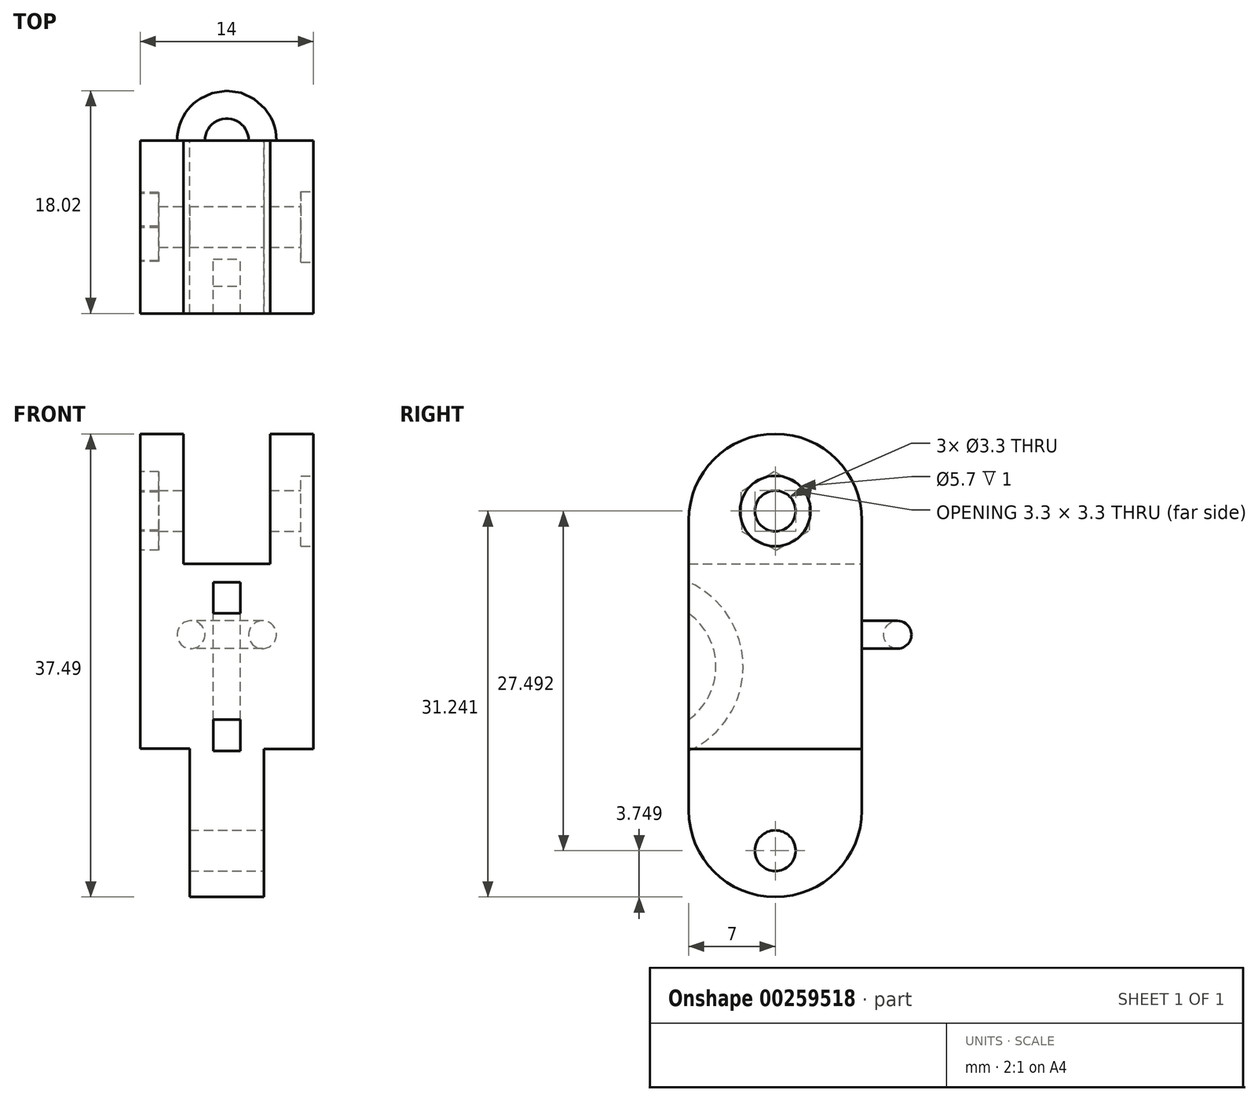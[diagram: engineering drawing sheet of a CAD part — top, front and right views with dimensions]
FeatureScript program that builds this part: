
annotation { "Feature Type Name" : "Feature", "Feature Type Description" : "" }
export const myFeature = defineFeature(function(context is Context, id is Id, definition is map)
    precondition{}
    {
        {
            var Q0;
            Q0=qCreatedBy(makeId("Front.planeOp"),FACE);
            var sketch = newSketch(context, id + "F0", { "sketchPlane" : qUnion([Q0])});
            skLineSegment(sketch, "E0.left", {"start": v(-39.5, 21.54) * mm, "end": v(-39.5, -1.95) * mm});
            skLineSegment(sketch, "E0.right", {"start": v(-25.5, 21.54) * mm, "end": v(-25.5, -1.98) * mm});
            skLineSegment(sketch, "E1.left", {"start": v(-39.5, 21.54) * mm, "end": v(-39.5, 21.54) * mm});
            skLineSegment(sketch, "E2", {"start": v(-36, 21.54) * mm, "end": v(-36, 13.03) * mm});
            skLineSegment(sketch, "E3", {"start": v(-36, 13.03) * mm, "end": v(-29, 13.03) * mm});
            skLineSegment(sketch, "E4", {"start": v(-29, 13.03) * mm, "end": v(-29, 21.53) * mm});
            skPoint(sketch, "E5", {"position": v(-29, 17.28) * mm});
            skLineSegment(sketch, "E6", {"start": v(-35.5, -6.45) * mm, "end": v(-35.5, -13.95) * mm});
            skLineSegment(sketch, "E7", {"start": v(-35.5, -13.95) * mm, "end": v(-29.5, -13.95) * mm});
            skLineSegment(sketch, "E8", {"start": v(-29.5, -13.95) * mm, "end": v(-29.5, -6.48) * mm});
            skLineSegment(sketch, "E9", {"start": v(-35.5, -6.45) * mm, "end": v(-29.5, -6.48) * mm});
            skLineSegment(sketch, "E10", {"start": v(-35.5, -3.45) * mm, "end": v(-35.5, -6.45) * mm});
            skLineSegment(sketch, "E11", {"start": v(-29.5, -6.48) * mm, "end": v(-29.5, -3.48) * mm});
            skPoint(sketch, "E12", {"position": v(-29.5, -10.22) * mm});
            skLineSegment(sketch, "E13", {"start": v(-39.5, 21.54) * mm, "end": v(-39.5, 23.54) * mm});
            skLineSegment(sketch, "E14", {"start": v(-36, 21.54) * mm, "end": v(-36, 23.54) * mm});
            skLineSegment(sketch, "E15", {"start": v(-36, 23.54) * mm, "end": v(-39.5, 23.54) * mm});
            skLineSegment(sketch, "E16", {"start": v(-29, 21.53) * mm, "end": v(-29, 23.54) * mm});
            skLineSegment(sketch, "E17", {"start": v(-25.5, 21.54) * mm, "end": v(-25.5, 23.54) * mm});
            skLineSegment(sketch, "E18", {"start": v(-25.5, 23.54) * mm, "end": v(-29, 23.54) * mm});
            skLineSegment(sketch, "E19", {"start": v(-35.5, -3.45) * mm, "end": v(-35.5, -1.95) * mm});
            skLineSegment(sketch, "E20", {"start": v(-35.5, -1.95) * mm, "end": v(-39.5, -1.95) * mm});
            skLineSegment(sketch, "E21", {"start": v(-29.5, -3.48) * mm, "end": v(-29.5, -1.98) * mm});
            skLineSegment(sketch, "E22", {"start": v(-29.5, -1.98) * mm, "end": v(-25.5, -1.98) * mm});
            skSolve(sketch);
        }
        {
            var Q0;
            Q0=makeQuery(id+"F0.imprint","IMPRINT",FACE,{"disambiguationData":[TD([[makeQuery(id+"F0.imprint","IMPRINT",EDGE,{"derivedFrom":sQuery(id+"F0.wireOp",EDGE,"E0.top")}),1.0]])]});
            var Q1;
            Q1=makeQuery(id+"F0.imprint","IMPRINT",FACE,{"disambiguationData":[TD([[makeQuery(id+"F0.imprint","IMPRINT",EDGE,{"derivedFrom":sQuery(id+"F0.wireOp",EDGE,"ADavjHGe-tSKU-QmEj-BJW0-Q7HaZQKlhmP1")}),1.0]])]});
            var Q2;
            Q2=makeQuery(id+"F0.imprint","IMPRINT",FACE,{"disambiguationData":[TD([[makeQuery(id+"F0.imprint","IMPRINT",EDGE,{"derivedFrom":sQuery(id+"F0.wireOp",EDGE,"E0.left")}),1.0]])]});
            var Q3;
            Q3=makeQuery(id+"F0.imprint","IMPRINT",FACE,{"disambiguationData":[TD([[makeQuery(id+"F0.imprint","IMPRINT",EDGE,{"derivedFrom":sQuery(id+"F0.wireOp",EDGE,"E6")}),1.0]])]});
            extrude(context, id + "F1", {"entities" : qUnion([Q0, Q1, Q2, Q3]), "endBound" : BoundingType.SYMMETRIC, "depth" : 14 * mm});
        }
        {
            var Q0;
            Q0=makeQuery(id+"F1.opExtrude","SWEPT_FACE",FACE,{"disambiguationData":[OSD([sQuery(id+"F0.wireOp",EDGE,"E8")])]});
            var sketch = newSketch(context, id + "F2", { "sketchPlane" : qUnion([Q0])});
            skCircle(sketch, "E23", {"center": v(0, -10.2) * mm, "radius": 1.65 * mm});
            skSolve(sketch);
        }
        {
            var Q0;
            Q0 = qSketchRegion(id + "F2", true);
            extrude(context, id + "F3", {"entities" : qUnion([Q0]), "operationType" : NewBodyOperationType.REMOVE, "oppositeDirection" : true, "depth" : 25 * mm});
        }
        {
            var Q0;
            Q0=makeQuery(id+"F1.opExtrude","SWEPT_FACE",FACE,{"disambiguationData":[OSD([sQuery(id+"F0.wireOp",EDGE,"E0.right")])]});
            var sketch = newSketch(context, id + "F4", { "sketchPlane" : qUnion([Q0])});
            skCircle(sketch, "E24", {"center": v(0, 17.3) * mm, "radius": 1.65 * mm});
            skSolve(sketch);
        }
        {
            var Q0;
            Q0 = qSketchRegion(id + "F4", true);
            extrude(context, id + "F5", {"entities" : qUnion([Q0]), "operationType" : NewBodyOperationType.REMOVE, "oppositeDirection" : true, "depth" : 25 * mm});
        }
        {
            var Q0;
            Q0=makeQuery(id+"F1.opExtrude","CAP_EDGE",EDGE,{"disambiguationData":[OSD([sQuery(id+"F0.wireOp",EDGE,"E15")])],"isStart":false});
            var Q1;
            Q1=makeQuery(id+"F1.opExtrude","CAP_EDGE",EDGE,{"disambiguationData":[OSD([sQuery(id+"F0.wireOp",EDGE,"E15")])],"isStart":true});
            var Q2;
            Q2=makeQuery(id+"F1.opExtrude","CAP_EDGE",EDGE,{"disambiguationData":[OSD([sQuery(id+"F0.wireOp",EDGE,"E18")])],"isStart":true});
            var Q3;
            Q3=makeQuery(id+"F1.opExtrude","CAP_EDGE",EDGE,{"disambiguationData":[OSD([sQuery(id+"F0.wireOp",EDGE,"E18")])],"isStart":false});
            var Q4;
            Q4=makeQuery(id+"F1.opExtrude","CAP_EDGE",EDGE,{"disambiguationData":[OSD([sQuery(id+"F0.wireOp",EDGE,"E7")])],"isStart":false});
            var Q5;
            Q5=makeQuery(id+"F1.opExtrude","CAP_EDGE",EDGE,{"disambiguationData":[OSD([sQuery(id+"F0.wireOp",EDGE,"E7")])],"isStart":true});
            fillet(context, id + "F6", {"entities" : qUnion([Q0, Q1, Q2, Q3, Q4, Q5]), "radius" : 7 * mm, "tangentPropagation" : true, "allowEdgeOverflow" : false});
        }
        {
            var Q0;
            Q0=makeQuery(id+"F1.opExtrude","SWEPT_FACE",FACE,{"disambiguationData":[OSD([sQuery(id+"F0.wireOp",EDGE,"E0.right")])]});
            var sketch = newSketch(context, id + "F7", { "sketchPlane" : qUnion([Q0])});
            skCircle(sketch, "E25", {"center": v(0, 17.3) * mm, "radius": 2.85 * mm});
            skSolve(sketch);
        }
        {
            var Q0;
            Q0 = qSketchRegion(id + "F7", true);
            extrude(context, id + "F8", {"entities" : qUnion([Q0]), "operationType" : NewBodyOperationType.REMOVE, "oppositeDirection" : true, "depth" : 1 * mm});
        }
        {
            var Q0;
            Q0=makeQuery(id+"F1.opExtrude","SWEPT_FACE",FACE,{"disambiguationData":[OSD([sQuery(id+"F0.wireOp",EDGE,"E0.left")])]});
            var sketch = newSketch(context, id + "F9", { "sketchPlane" : qUnion([Q0])});
            skCircle(sketch, "E26.cCircle", {"center": v(0, 17.3) * mm, "radius": 2.75 * mm, "construction": true});
            skLineSegment(sketch, "E26.0", {"start": v(2.72, 15.64) * mm, "end": v(-0.07, 14.12) * mm});
            skLineSegment(sketch, "E26.1", {"start": v(-0.07, 14.12) * mm, "end": v(-2.78, 15.76) * mm});
            skLineSegment(sketch, "E26.2", {"start": v(-2.78, 15.76) * mm, "end": v(-2.72, 18.94) * mm});
            skLineSegment(sketch, "E26.3", {"start": v(-2.72, 18.94) * mm, "end": v(0.07, 20.47) * mm});
            skLineSegment(sketch, "E26.4", {"start": v(0.07, 20.47) * mm, "end": v(2.78, 18.82) * mm});
            skLineSegment(sketch, "E26.5", {"start": v(2.78, 18.82) * mm, "end": v(2.72, 15.64) * mm});
            skPoint(sketch, "E26.0.midPoint", {"position": v(1.32, 14.88) * mm});
            skSolve(sketch);
        }
        {
            var Q0;
            Q0 = qSketchRegion(id + "F9", true);
            extrude(context, id + "F10", {"entities" : qUnion([Q0]), "operationType" : NewBodyOperationType.REMOVE, "oppositeDirection" : true, "depth" : 1.5 * mm});
        }
        {
            var Q0;
            Q0=makeQuery(id+"F1.opExtrude","CAP_FACE",FACE,{"disambiguationData":[OSD([sQuery(id+"F0.wireOp",EDGE,"E0.left"),sQuery(id+"F0.wireOp",EDGE,"E0.right"),sQuery(id+"F0.wireOp",EDGE,"E2"),sQuery(id+"F0.wireOp",EDGE,"E3"),sQuery(id+"F0.wireOp",EDGE,"E4"),sQuery(id+"F0.wireOp",EDGE,"E6"),sQuery(id+"F0.wireOp",EDGE,"E7"),sQuery(id+"F0.wireOp",EDGE,"E8"),sQuery(id+"F0.wireOp",EDGE,"E10"),sQuery(id+"F0.wireOp",EDGE,"E11"),sQuery(id+"F0.wireOp",EDGE,"E13"),sQuery(id+"F0.wireOp",EDGE,"E14"),sQuery(id+"F0.wireOp",EDGE,"E15"),sQuery(id+"F0.wireOp",EDGE,"E16"),sQuery(id+"F0.wireOp",EDGE,"E17"),sQuery(id+"F0.wireOp",EDGE,"E18"),sQuery(id+"F0.wireOp",EDGE,"E19"),sQuery(id+"F0.wireOp",EDGE,"E20"),sQuery(id+"F0.wireOp",EDGE,"E21"),sQuery(id+"F0.wireOp",EDGE,"E22")])],"isStart":false});
            var sketch = newSketch(context, id + "F11", { "sketchPlane" : qUnion([Q0])});
            skLineSegment(sketch, "E27", {"start": v(-32.5, 13.03) * mm, "end": v(-32.5, -6.95) * mm});
            skPoint(sketch, "E28.orphan", {"position": v(-39.5, 7.3) * mm});
            skCircle(sketch, "E29", {"center": v(-35.5, 7.3) * mm, "radius": 1.13 * mm});
            skPoint(sketch, "E30.orphan", {"position": v(-25.5, 7.3) * mm});
            skPoint(sketch, "E31.orphan", {"position": v(-32.5, 7.3) * mm});
            skSolve(sketch);
        }
        {
            var Q0;
            Q0=makeQuery(id+"F11.imprint","IMPRINT",FACE,{"disambiguationData":[TD([[makeQuery(id+"F11.imprint","IMPRINT",EDGE,{"derivedFrom":sQuery(id+"F11.wireOp",EDGE,"E29")}),1.0]])]});
            var Q1;
            Q1=sQuery(id+"F11.wireOp",EDGE,"E27");
            revolve(context, id + "F12", {"operationType" : NewBodyOperationType.ADD, "entities" : qUnion([Q0]), "axis" : qUnion([Q1]), "revolveType" : RevolveType.FULL});
        }
        {
            var Q0;
            Q0=makeQuery(id+"F1.opExtrude","CAP_FACE",FACE,{"disambiguationData":[OSD([sQuery(id+"F0.wireOp",EDGE,"E0.left"),sQuery(id+"F0.wireOp",EDGE,"E0.right"),sQuery(id+"F0.wireOp",EDGE,"E2"),sQuery(id+"F0.wireOp",EDGE,"E3"),sQuery(id+"F0.wireOp",EDGE,"E4"),sQuery(id+"F0.wireOp",EDGE,"E6"),sQuery(id+"F0.wireOp",EDGE,"E7"),sQuery(id+"F0.wireOp",EDGE,"E8"),sQuery(id+"F0.wireOp",EDGE,"E10"),sQuery(id+"F0.wireOp",EDGE,"E11"),sQuery(id+"F0.wireOp",EDGE,"E13"),sQuery(id+"F0.wireOp",EDGE,"E14"),sQuery(id+"F0.wireOp",EDGE,"E15"),sQuery(id+"F0.wireOp",EDGE,"E16"),sQuery(id+"F0.wireOp",EDGE,"E17"),sQuery(id+"F0.wireOp",EDGE,"E18"),sQuery(id+"F0.wireOp",EDGE,"E19"),sQuery(id+"F0.wireOp",EDGE,"E20"),sQuery(id+"F0.wireOp",EDGE,"E21"),sQuery(id+"F0.wireOp",EDGE,"E22")])],"isStart":true});
            var sketch = newSketch(context, id + "F13", { "sketchPlane" : qUnion([Q0])});
            skLineSegment(sketch, "E32", {"start": v(32.5, 13.03) * mm, "end": v(32.5, -6.95) * mm});
            skPoint(sketch, "E33.orphan", {"position": v(39.5, 7.28) * mm});
            skPoint(sketch, "E34.orphan", {"position": v(25.5, 7.28) * mm});
            skCircle(sketch, "E35", {"center": v(29.6, 7.28) * mm, "radius": 1.13 * mm});
            skPoint(sketch, "E36.end.orphan", {"position": v(32.5, 7.28) * mm});
            skSolve(sketch);
        }
        {
            var Q0;
            Q0=makeQuery(id+"F13.imprint","IMPRINT",FACE,{"disambiguationData":[TD([[makeQuery(id+"F13.imprint","IMPRINT",EDGE,{"derivedFrom":sQuery(id+"F13.wireOp",EDGE,"E35")}),1.0]])]});
            var Q1;
            Q1=sQuery(id+"F13.wireOp",EDGE,"E32");
            revolve(context, id + "F14", {"operationType" : NewBodyOperationType.ADD, "entities" : qUnion([Q0]), "axis" : qUnion([Q1]), "revolveType" : RevolveType.FULL});
        }
        {
            var Q0;
            Q0=makeQuery(id+"F1.opExtrude","SWEPT_FACE",FACE,{"disambiguationData":[OSD([sQuery(id+"F0.wireOp",EDGE,"E3")])]});
            var sketch = newSketch(context, id + "F15", { "sketchPlane" : qUnion([Q0])});
            skLineSegment(sketch, "E37", {"start": v(-29, -7) * mm, "end": v(-25.5, -7) * mm});
            skLineSegment(sketch, "E38", {"start": v(-36, -7) * mm, "end": v(-29, -7) * mm});
            skLineSegment(sketch, "E39", {"start": v(-39.5, -7) * mm, "end": v(-36, -7) * mm});
            skLineSegment(sketch, "E40.bottom", {"start": v(-39.5, -7) * mm, "end": v(-25.5, -7) * mm});
            skLineSegment(sketch, "E40.top", {"start": v(-39.5, -13.43) * mm, "end": v(-25.5, -13.43) * mm});
            skLineSegment(sketch, "E40.left", {"start": v(-39.5, -7) * mm, "end": v(-39.5, -13.43) * mm});
            skLineSegment(sketch, "E40.right", {"start": v(-25.5, -7) * mm, "end": v(-25.5, -13.43) * mm});
            skSolve(sketch);
        }
        {
            var Q0;
            Q0=makeQuery(id+"F15.imprint","IMPRINT",FACE,{"disambiguationData":[TD([[makeQuery(id+"F15.imprint","IMPRINT",EDGE,{"derivedFrom":sQuery(id+"F15.wireOp",EDGE,"E40.top")}),1.0]])]});
            extrude(context, id + "F16", {"entities" : qUnion([Q0]), "operationType" : NewBodyOperationType.REMOVE, "oppositeDirection" : true, "depth" : 25 * mm});
        }
        {
            var Q0;
            Q0=qCreatedBy(makeId("Right.planeOp"),FACE);
            cPlane(context, id + "F17", {"entities" : qUnion([Q0]), "cplaneType" : CPlaneType.OFFSET, "offset" : 32.5 * mm, "oppositeDirection" : true, "width" : 150 * mm, "height" : 150 * mm});
        }
        {
            var Q0;
            Q0=qCreatedBy(id+"F17.planeOp",FACE);
            var sketch = newSketch(context, id + "F18", { "sketchPlane" : qUnion([Q0])});
            skArc(sketch, "E41", {"start": v(-7, 0.4) * mm, "mid": v(-4.8, 4.7) * mm, "end": v(-7, 9) * mm});
            skArc(sketch, "E42", {"start": v(-7, -2.13) * mm, "mid": v(-2.6, 4.7) * mm, "end": v(-7, 11.53) * mm});
            skLineSegment(sketch, "E43", {"start": v(-7, 13.03) * mm, "end": v(-7, 9) * mm});
            skLineSegment(sketch, "E44.trimOffspring", {"start": v(-7, 0.4) * mm, "end": v(-7, -2.13) * mm});
            skPoint(sketch, "E45.orphan", {"position": v(-7, -6.95) * mm});
            skSolve(sketch);
        }
        {
            var Q0;
            Q0 = qSketchRegion(id + "F18", true);
            extrude(context, id + "F19", {"entities" : qUnion([Q0]), "operationType" : NewBodyOperationType.REMOVE, "endBound" : BoundingType.SYMMETRIC, "oppositeDirection" : true, "depth" : 2.2 * mm});
        }
    });
